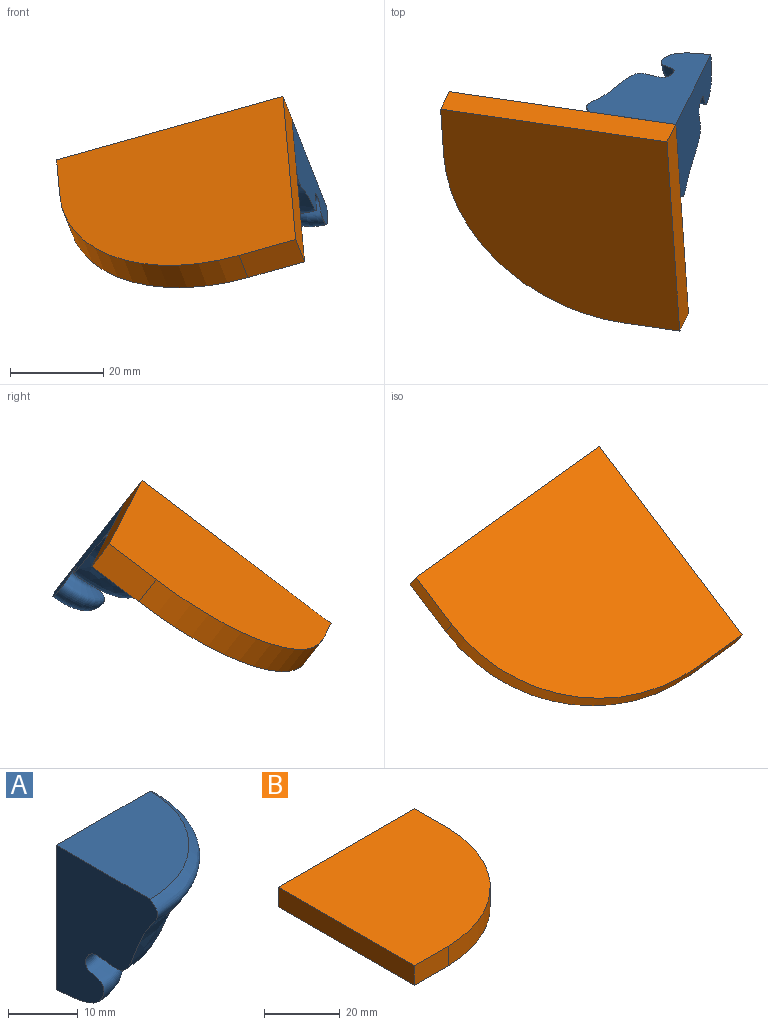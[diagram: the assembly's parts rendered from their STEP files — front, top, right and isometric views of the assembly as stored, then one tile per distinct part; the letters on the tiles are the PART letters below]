
ASSEMBLY  parts=2 mates=1
PART A: 4 faces, bbox 21x21x25.4 mm
  f0: revolved ~25.4x20.59mm, area 790.2mm2, adj f1,f2,f3
  f1: plane 19.05x19.05mm, normal (0,0,1), area 285mm2, adj f0,f2,f3
  f2: plane 25.4x20.96mm, normal (-1,0,0), area 344.6mm2, adj f0,f1,f3
  f3: plane 25.4x20.96mm, normal (0,1,0), area 344.6mm2, adj f0,f1,f2
PART B: 7 faces, bbox 50.8x50.8x6.4 mm
  f0: plane 12.7x6.35mm, normal (0,-1,0), area 80.6mm2, adj f1,f4,f5,f6
  f1: cylinder r=38.1mm len=38.1mm, axis (0,0,-1), area 380mm2, adj f0,f2,f5,f6
  f2: plane 12.7x6.35mm, normal (1,0,0), area 80.6mm2, adj f1,f3,f5,f6
  f3: plane 50.8x6.35mm, normal (0,1,0), area 322.6mm2, adj f2,f4,f5,f6
  f4: plane 50.8x6.35mm, normal (-1,0,0), area 322.6mm2, adj f0,f3,f5,f6
  f5: plane 50.8x50.8mm, normal (0,0,1), area 2269.1mm2, adj f0,f1,f2,f3,f4
  f6: plane 50.8x50.8mm, normal (0,0,-1), area 2269.1mm2, adj f0,f1,f2,f3,f4
PLACE A rot(axis=(0.43,0.16,-0.89),99.6deg) t=(-27.24,35.33,-55.85)mm
PLACE B rot(axis=(0.43,0.16,-0.89),99.6deg) t=(-85.24,17.77,-58.67)mm
MATE fastened A.f1 <-> B.f6  axis (-0.3,-0.59,0.75) through (-36.54,46.8,-16.75)mm
